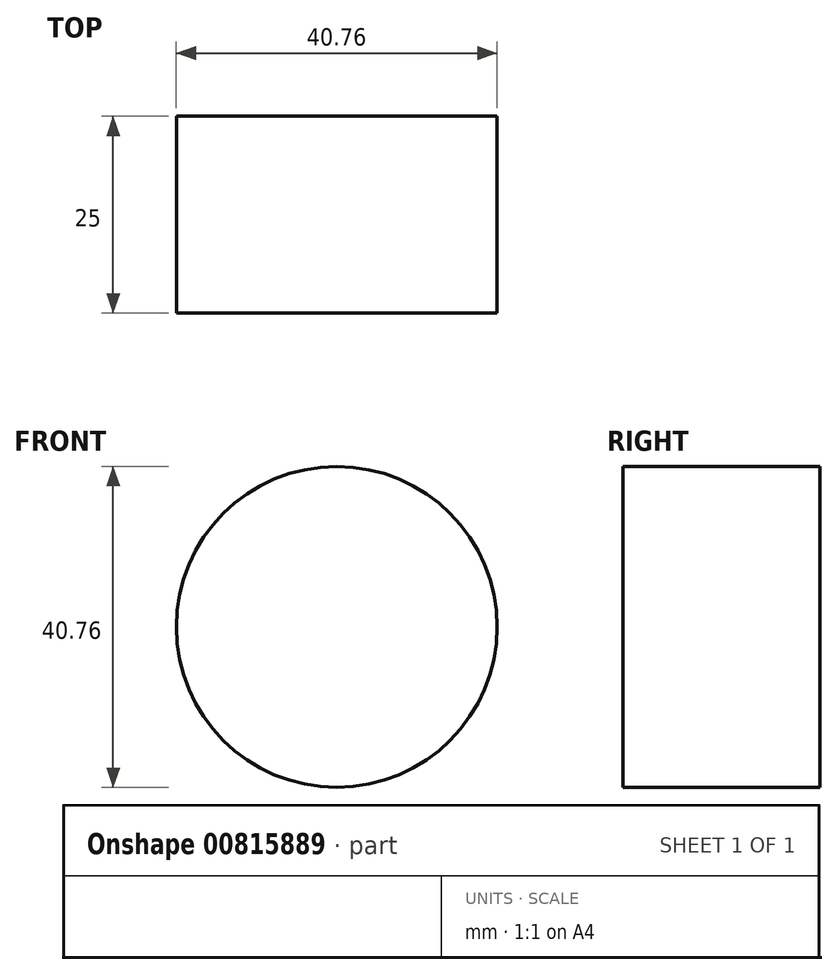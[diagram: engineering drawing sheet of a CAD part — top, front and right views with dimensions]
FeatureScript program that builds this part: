
annotation { "Feature Type Name" : "Feature", "Feature Type Description" : "" }
export const myFeature = defineFeature(function(context is Context, id is Id, definition is map)
    precondition{}
    {
        {
            var Q0;
            Q0=qCreatedBy(makeId("Front.planeOp"),FACE);
            var sketch = newSketch(context, id + "F0", { "sketchPlane" : qUnion([Q0])});
            skCircle(sketch, "E0", {"center": v(0, 0) * mm, "radius": 20.38 * mm});
            skSolve(sketch);
        }
        {
            var Q0;
            Q0 = qSketchRegion(id + "F0", true);
            extrude(context, id + "F1", {"entities" : qUnion([Q0]), "depth" : 25 * mm, "offsetDistance" : 25 * mm});
        }
    });
